# Revit family: 514421930067
name_source: partatom
category: Plumbing Fixtures
revit_build: Autodesk Revit 2018 (Build: 20170223_1515(x64)
units: mm (PartAtom-declared; Revit-internal decimal feet)

## family parameters
Always vertical = Yes
Cut with Voids When Loaded = No
OmniClass Number = 23.45.55.00
OmniClass Title = Sanitary Faucets, Wastes
Part Type = Normal
Room Calculation Point = No
Round Connector Dimension = Use Diameter
Shared = No
Work Plane-Based = No

## types (1)
- 514421930067 Bath and shower faucet
    2D/3D/BIM Files URL = http://static.hansa.com
    3D View = https://static.hansa.com
    Advanced Features = Inner body made of DZR brass
    Aerator = Standard aerator
    AssetType = Fixed
    BIMObjectName = 514421930067
    Backflow Prevention EN1717 = EB
    BodyMaterial = Brass
    Brand = HANSA
    Catalog Drawing URL = http://static.hansa.com
    Category = Bathroom
    CloseOffRating = 0
    Color = Chrome
    Connection = Eccentric coupling(s)
    Connection Size = G3/4
    Dimension Drawing URL = http://static.hansa.com
    Diverter = Pull operated diverter;Automatic reset
    DurationUnit = Year
    EAN Number = 4057304002946
    EN Standard = EN 817
    ETIM Class Number = EC010862 Bath mixing tap
    Eco Flow At 300kPa = 0.2 L/s
    FDV Document URL = http://www.hansa.com
    FaucetMainMaterial = Brass
    Features = Single-lever
    Finish = Polished
    Flow Drawing URL = http://static.hansa.com
    Flow Rate At 300kPa = 340.3 L/s
    FlowCoefficient = 0
    Group = Bath and shower faucet
    IfcExportAs = IfcValveType
    IfcExportType = FAUCET
    Installation Type = Wall mounted
    Installation Width = CC150 ± 15 mm
    Installation and Maintenance Guide URL = http://static.hansa.com
    Interactive AR View URL = https://static.hansa.com
    Lever Handle = Hot/Cold symbols;Single operating lever/handle
    Manufacturer = HANSA
    ManufacturerName = HANSA
    ManufacturerURL = http://www.hansa.com
    Market = Belgium;Czech Republic;Spain;France;International;Italy;Netherlands;Slovakia
    Material = Brass
    Max. Hot Water Supply = 90 °C
    Mechanical Parts = Non-return valve(s);ø 35 mm ceramic eco cartridge for flow and temperature control
    Mobile Product Information URL = http://mpi.hansa.com
    Model = 514421930067 Bath and shower faucet
    ModelReference = 514421930067
    NBSDescription = Water supply fittings for baths
    NBSReference = 45-35-70/315
    Name = 514421930067 Bath and shower faucet
    Name_en = 514421930067 Bath and shower faucet
    Noise Class = I (ISO 3822)
    NominalDepth = 179 mm
    NominalHeight = 122 mm  [stored 0.400262 ft]
    NominalWidth = 220 mm
    Product Code = 514421930067
    Product Family = HANSAPOLO
    Product Image URL = http://static.hansa.com
    Product URL = http://static.hansa.com
    Revision = 3
    Sales Package dimensions (LxWxH) = 210 x 176 x 162
    Shape = Sculptured
    Size = 220x180x122 mm
    Spare-Part Information URL = http://static.hansa.com
    Spout Projection = 159 mm
    Surface treatment = Chrome
    Technical DataSheet URL = http://www.hansa.com
    Temperature = Temperature limiter
    Temperature Adjustments = Limitation option for maximum temperature and flow-rate ;Energy saving variation - cold water in the middle position
    UNSPSC Class Number = 30181700 Faucets or taps
    URL Declaration of Conformity = http://static.hansa.com
    URL REACH = http://static.hansa.com
    Uniclass2 = Pr_40_30_96_07
    Uniclass2015Description = Bath manual water supply sets
    Uniclass2015Reference = Pr_40_20_87_07
    Version = 3
    VersionDate = 01/07/2022
    Warranty Information URL = http://warranty.hansa.com
    WarrantyDescription = http://warranty.hansa.com
    WarrantyDurationUnit = Year
    Working Pressure = 50 - 1000 kPa
    WorkingPressure = 50 - 1000 kPa

note: [stored X ft] marks values corroborated as IEEE doubles in the binary element streams (Revit-internal decimal feet)

## geometry (parser evidence)
native form markers: Sweep x5
no freeform markers — native parametric forms only
